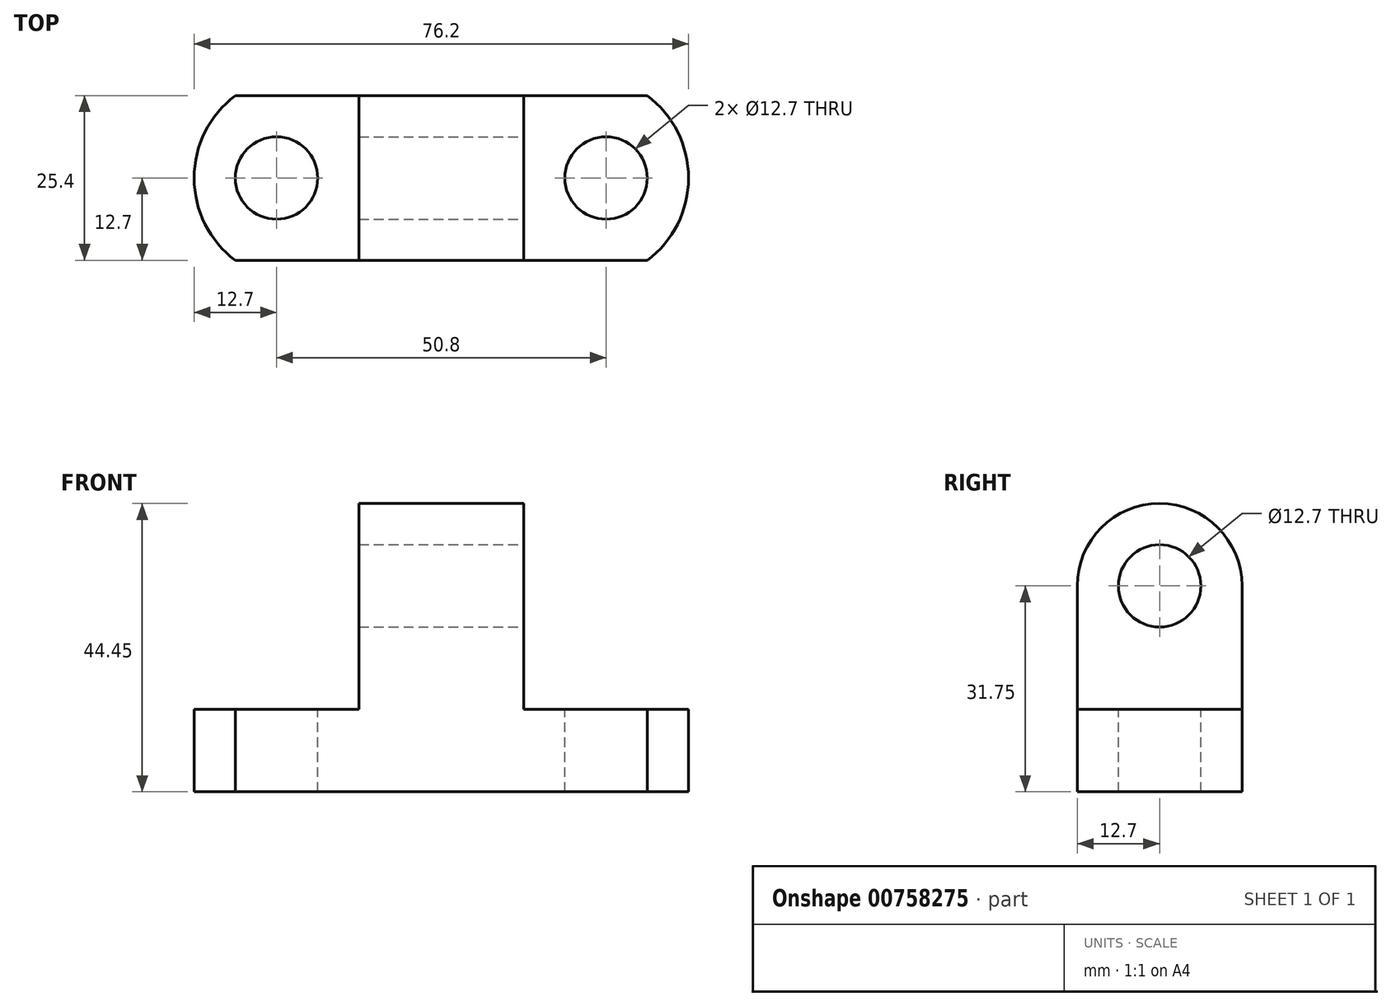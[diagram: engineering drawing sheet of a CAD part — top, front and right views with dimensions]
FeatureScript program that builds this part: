
annotation { "Feature Type Name" : "Feature", "Feature Type Description" : "" }
export const myFeature = defineFeature(function(context is Context, id is Id, definition is map)
    precondition{}
    {
        {
            var Q0;
            Q0=qCreatedBy(makeId("Front.planeOp"),FACE);
            var sketch = newSketch(context, id + "F0", { "sketchPlane" : qUnion([Q0])});
            skLineSegment(sketch, "E0", {"start": v(0, 0) * mm, "end": v(76.2, 0) * mm});
            skLineSegment(sketch, "E1", {"start": v(76.2, 0) * mm, "end": v(76.2, 44.45) * mm});
            skLineSegment(sketch, "E2", {"start": v(76.2, 44.45) * mm, "end": v(0, 44.45) * mm});
            skLineSegment(sketch, "E3", {"start": v(0, 44.45) * mm, "end": v(0, 0) * mm});
            skSolve(sketch);
        }
        {
            var Q0;
            Q0 = qSketchRegion(id + "F0", true);
            extrude(context, id + "F1", {"entities" : qUnion([Q0]), "depth" : 25.4 * mm, "offsetDistance" : 25.4 * mm});
        }
        {
            var Q0;
            Q0=makeQuery(id+"F1.opExtrude","SWEPT_FACE",FACE,{"disambiguationData":[OSD([sQuery(id+"F0.wireOp",EDGE,"E2")])]});
            var sketch = newSketch(context, id + "F2", { "sketchPlane" : qUnion([Q0])});
            skLineSegment(sketch, "E4", {"start": v(50.8, 0) * mm, "end": v(50.8, -25.4) * mm});
            skLineSegment(sketch, "E5", {"start": v(25.4, 0) * mm, "end": v(25.4, -25.4) * mm});
            skSolve(sketch);
        }
        {
            var Q0;
            {var subQ0=sQuery(id+"F2.wireOp",EDGE,"E4");Q0=makeQuery(id+"F2.imprint","IMPRINT",FACE,{"disambiguationData":[TD([[makeQuery(id+"F2.imprint","IMPRINT",EDGE,{"derivedFrom":subQ0}),1.0]])]});}
            var Q1;
            {var subQ0=sQuery(id+"F2.wireOp",EDGE,"E5");Q1=makeQuery(id+"F2.imprint","IMPRINT",FACE,{"disambiguationData":[TD([[makeQuery(id+"F2.imprint","IMPRINT",EDGE,{"derivedFrom":subQ0}),-1.0]])]});}
            extrude(context, id + "F3", {"entities" : qUnion([Q0, Q1]), "operationType" : NewBodyOperationType.REMOVE, "oppositeDirection" : true, "depth" : 31.75 * mm, "offsetDistance" : 25.4 * mm});
        }
        {
            var Q0;
            Q0=makeQuery(id+"F3.boolean.opBoolean","COPY",FACE,{"derivedFrom":makeQuery(id+"F3.opExtrude","CAP_FACE",FACE,{"disambiguationData":[OSD([sQuery(id+"F0.wireOp",EDGE,"E1"),sQuery(id+"F0.wireOp",EDGE,"E2"),sQuery(id+"F2.wireOp",EDGE,"E4")])],"isStart":false})});
            var sketch = newSketch(context, id + "F4", { "sketchPlane" : qUnion([Q0])});
            skCircle(sketch, "E6", {"center": v(63.5, -12.7) * mm, "radius": 6.35 * mm});
            skCircle(sketch, "E7", {"center": v(12.7, -12.7) * mm, "radius": 6.35 * mm});
            skSolve(sketch);
        }
        {
            var Q0;
            Q0=makeQuery(id+"F4.imprint","IMPRINT",FACE,{"disambiguationData":[TD([[makeQuery(id+"F4.imprint","IMPRINT",EDGE,{"derivedFrom":sQuery(id+"F4.wireOp",EDGE,"E7")}),1.0]])]});
            var Q1;
            Q1=makeQuery(id+"F4.imprint","IMPRINT",FACE,{"disambiguationData":[TD([[makeQuery(id+"F4.imprint","IMPRINT",EDGE,{"derivedFrom":sQuery(id+"F4.wireOp",EDGE,"E6")}),1.0]])]});
            extrude(context, id + "F5", {"entities" : qUnion([Q0, Q1]), "operationType" : NewBodyOperationType.REMOVE, "oppositeDirection" : true, "depth" : 25.4 * mm, "offsetDistance" : 25.4 * mm});
        }
        {
            var Q0;
            Q0=makeQuery(id+"F3.boolean.opBoolean","COPY",FACE,{"derivedFrom":makeQuery(id+"F3.opExtrude","SWEPT_FACE",FACE,{"disambiguationData":[OSD([sQuery(id+"F2.wireOp",EDGE,"E4")])]})});
            var sketch = newSketch(context, id + "F6", { "sketchPlane" : qUnion([Q0])});
            skCircle(sketch, "E8", {"center": v(-12.7, 31.75) * mm, "radius": 6.35 * mm});
            skSolve(sketch);
        }
        {
            var Q0;
            Q0=makeQuery(id+"F6.imprint","IMPRINT",FACE,{"disambiguationData":[TD([[makeQuery(id+"F6.imprint","IMPRINT",EDGE,{"derivedFrom":sQuery(id+"F6.wireOp",EDGE,"E8")}),1.0]])]});
            extrude(context, id + "F7", {"entities" : qUnion([Q0]), "operationType" : NewBodyOperationType.REMOVE, "oppositeDirection" : true, "depth" : 25.4 * mm, "offsetDistance" : 25.4 * mm});
        }
        {
            var Q0;
            Q0=makeQuery(id+"F3.boolean.opBoolean","COPY",FACE,{"derivedFrom":makeQuery(id+"F3.opExtrude","CAP_FACE",FACE,{"disambiguationData":[OSD([sQuery(id+"F0.wireOp",EDGE,"E1"),sQuery(id+"F0.wireOp",EDGE,"E2"),sQuery(id+"F2.wireOp",EDGE,"E4")])],"isStart":false})});
            var sketch = newSketch(context, id + "F8", { "sketchPlane" : qUnion([Q0])});
            skArc(sketch, "E9", {"start": v(69.85, -25.4) * mm, "mid": v(76.2, -12.7) * mm, "end": v(69.85, 0) * mm});
            skSolve(sketch);
        }
        {
            var Q0;
            {var subQ0=sQuery(id+"F8.wireOp",EDGE,"E9");var subQ1=sQuery(id+"F0.wireOp",EDGE,"E2");var subQ3=sQuery(id+"F0.wireOp",EDGE,"E1");var subQ6=makeQuery(id+"F3.boolean.opBoolean","COPY",EDGE,{"derivedFrom":makeQuery(id+"F3.opExtrude","CAP_EDGE",EDGE,{"disambiguationData":[OSD([subQ3,subQ1])],"isStart":false})});var subQ7=makeQuery(id+"F8.imprint","INTERSECT",VERTEX,{"derivedFrom":[subQ6,subQ0]});Q0=makeQuery(id+"F8.imprint","IMPRINT",FACE,{"disambiguationData":[TD([[makeQuery(id+"F8.imprint","IMPRINT",EDGE,{"disambiguationData":[TD([[subQ7,-1.0]])],"derivedFrom":subQ0}),-1.0]])]});}
            var Q1;
            {var subQ0=sQuery(id+"F8.wireOp",EDGE,"E9");var subQ1=sQuery(id+"F0.wireOp",EDGE,"E2");var subQ3=sQuery(id+"F0.wireOp",EDGE,"E1");var subQ6=makeQuery(id+"F3.boolean.opBoolean","COPY",EDGE,{"derivedFrom":makeQuery(id+"F3.opExtrude","CAP_EDGE",EDGE,{"disambiguationData":[OSD([subQ3,subQ1])],"isStart":false})});var subQ7=makeQuery(id+"F8.imprint","INTERSECT",VERTEX,{"derivedFrom":[subQ6,subQ0]});Q1=makeQuery(id+"F8.imprint","IMPRINT",FACE,{"disambiguationData":[TD([[makeQuery(id+"F8.imprint","IMPRINT",EDGE,{"disambiguationData":[TD([[subQ7,1.0]])],"derivedFrom":subQ0}),-1.0]])]});}
            extrude(context, id + "F9", {"entities" : qUnion([Q0, Q1]), "operationType" : NewBodyOperationType.REMOVE, "oppositeDirection" : true, "depth" : 25.4 * mm, "offsetDistance" : 25.4 * mm});
        }
        {
            var Q0;
            Q0=makeQuery(id+"F3.boolean.opBoolean","COPY",FACE,{"derivedFrom":makeQuery(id+"F3.opExtrude","CAP_FACE",FACE,{"disambiguationData":[OSD([sQuery(id+"F0.wireOp",EDGE,"E2"),sQuery(id+"F0.wireOp",EDGE,"E3"),sQuery(id+"F2.wireOp",EDGE,"E5")])],"isStart":false})});
            var sketch = newSketch(context, id + "F10", { "sketchPlane" : qUnion([Q0])});
            skArc(sketch, "E10", {"start": v(6.35, 0) * mm, "mid": v(0, -12.7) * mm, "end": v(6.35, -25.4) * mm});
            skSolve(sketch);
        }
        {
            var Q0;
            {var subQ0=sQuery(id+"F10.wireOp",EDGE,"E10");var subQ1=sQuery(id+"F0.wireOp",EDGE,"E2");var subQ3=sQuery(id+"F0.wireOp",EDGE,"E3");var subQ6=makeQuery(id+"F3.boolean.opBoolean","COPY",EDGE,{"derivedFrom":makeQuery(id+"F3.opExtrude","CAP_EDGE",EDGE,{"disambiguationData":[OSD([subQ1,subQ3])],"isStart":false})});var subQ7=makeQuery(id+"F10.imprint","INTERSECT",VERTEX,{"derivedFrom":[subQ6,subQ0]});Q0=makeQuery(id+"F10.imprint","IMPRINT",FACE,{"disambiguationData":[TD([[makeQuery(id+"F10.imprint","IMPRINT",EDGE,{"disambiguationData":[TD([[subQ7,1.0]])],"derivedFrom":subQ0}),-1.0]])]});}
            var Q1;
            {var subQ0=sQuery(id+"F10.wireOp",EDGE,"E10");var subQ1=sQuery(id+"F0.wireOp",EDGE,"E2");var subQ3=sQuery(id+"F0.wireOp",EDGE,"E3");var subQ6=makeQuery(id+"F3.boolean.opBoolean","COPY",EDGE,{"derivedFrom":makeQuery(id+"F3.opExtrude","CAP_EDGE",EDGE,{"disambiguationData":[OSD([subQ1,subQ3])],"isStart":false})});var subQ7=makeQuery(id+"F10.imprint","INTERSECT",VERTEX,{"derivedFrom":[subQ6,subQ0]});Q1=makeQuery(id+"F10.imprint","IMPRINT",FACE,{"disambiguationData":[TD([[makeQuery(id+"F10.imprint","IMPRINT",EDGE,{"disambiguationData":[TD([[subQ7,-1.0]])],"derivedFrom":subQ0}),-1.0]])]});}
            extrude(context, id + "F11", {"entities" : qUnion([Q0, Q1]), "operationType" : NewBodyOperationType.REMOVE, "oppositeDirection" : true, "depth" : 25.4 * mm, "offsetDistance" : 25.4 * mm});
        }
        {
            var Q0;
            Q0=makeQuery(id+"F3.boolean.opBoolean","COPY",FACE,{"derivedFrom":makeQuery(id+"F3.opExtrude","SWEPT_FACE",FACE,{"disambiguationData":[OSD([sQuery(id+"F2.wireOp",EDGE,"E4")])]})});
            var sketch = newSketch(context, id + "F12", { "sketchPlane" : qUnion([Q0])});
            skArc(sketch, "E11", {"start": v(0, 31.75) * mm, "mid": v(-12.7, 44.45) * mm, "end": v(-25.4, 31.75) * mm});
            skSolve(sketch);
        }
        {
            var Q0;
            {var subQ0=sQuery(id+"F12.wireOp",EDGE,"E11");var subQ1=sQuery(id+"F2.wireOp",EDGE,"E4");var subQ5=makeQuery(id+"F3.boolean.opBoolean","COPY",EDGE,{"derivedFrom":makeQuery(id+"F3.opExtrude","CAP_EDGE",EDGE,{"disambiguationData":[OSD([subQ1])],"isStart":true})});var subQ6=makeQuery(id+"F12.imprint","INTERSECT",VERTEX,{"derivedFrom":[subQ5,subQ0]});Q0=makeQuery(id+"F12.imprint","IMPRINT",FACE,{"disambiguationData":[TD([[makeQuery(id+"F12.imprint","IMPRINT",EDGE,{"disambiguationData":[TD([[subQ6,-1.0]])],"derivedFrom":subQ0}),-1.0]])]});}
            var Q1;
            {var subQ0=sQuery(id+"F12.wireOp",EDGE,"E11");var subQ1=sQuery(id+"F2.wireOp",EDGE,"E4");var subQ5=makeQuery(id+"F3.boolean.opBoolean","COPY",EDGE,{"derivedFrom":makeQuery(id+"F3.opExtrude","CAP_EDGE",EDGE,{"disambiguationData":[OSD([subQ1])],"isStart":true})});var subQ6=makeQuery(id+"F12.imprint","INTERSECT",VERTEX,{"derivedFrom":[subQ5,subQ0]});Q1=makeQuery(id+"F12.imprint","IMPRINT",FACE,{"disambiguationData":[TD([[makeQuery(id+"F12.imprint","IMPRINT",EDGE,{"disambiguationData":[TD([[subQ6,1.0]])],"derivedFrom":subQ0}),-1.0]])]});}
            extrude(context, id + "F13", {"entities" : qUnion([Q0, Q1]), "operationType" : NewBodyOperationType.REMOVE, "oppositeDirection" : true, "depth" : 25.4 * mm, "offsetDistance" : 25.4 * mm});
        }
    });
